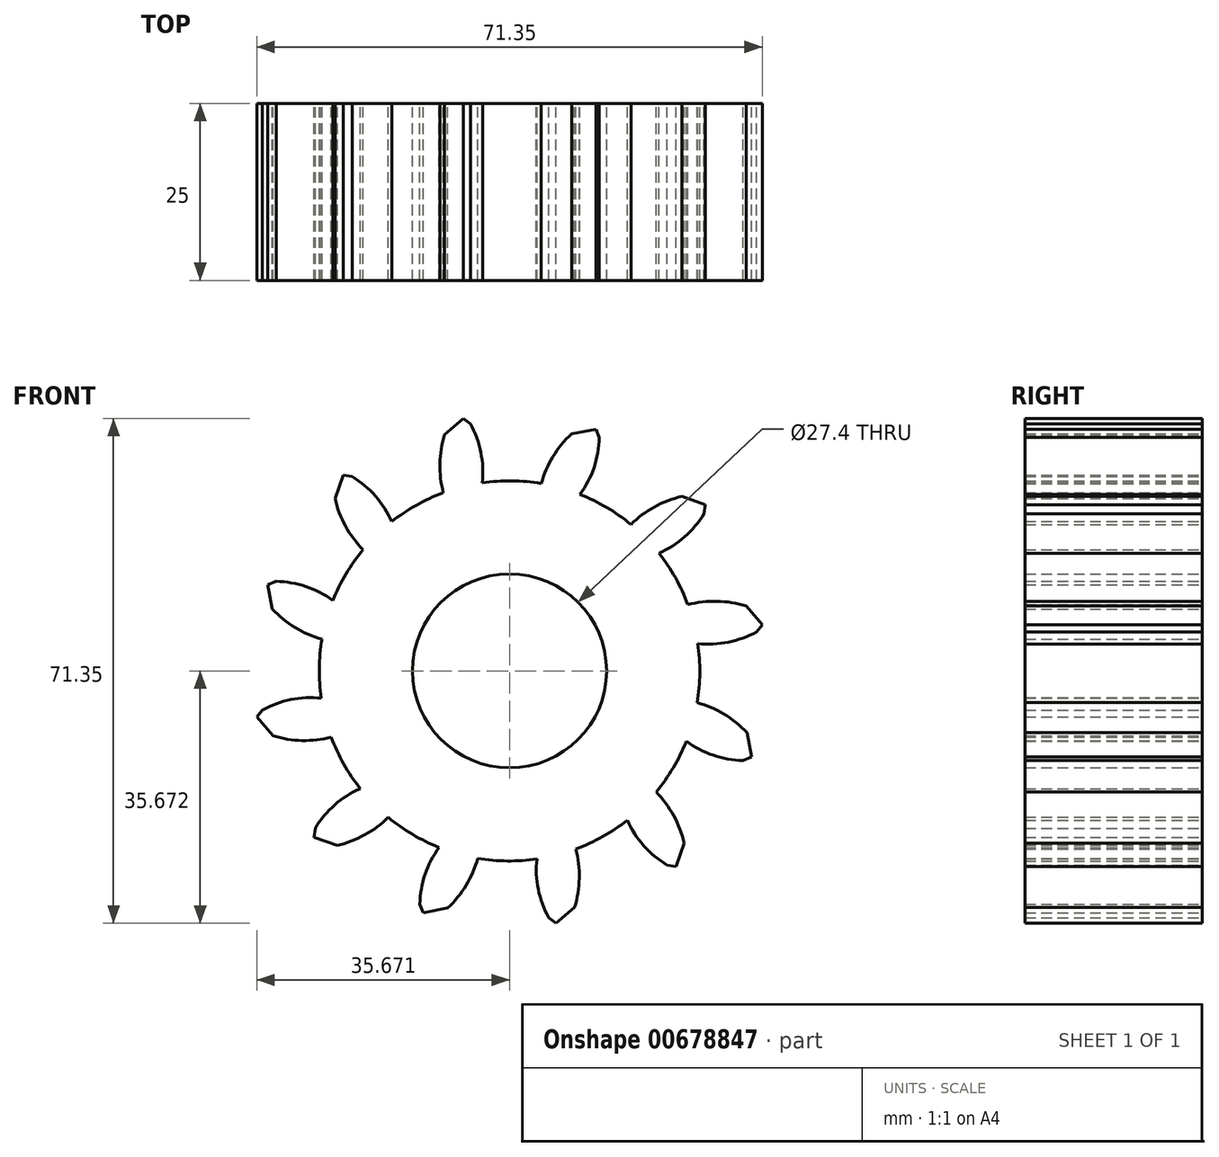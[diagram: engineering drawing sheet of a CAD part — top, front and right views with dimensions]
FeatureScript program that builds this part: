
annotation { "Feature Type Name" : "Feature", "Feature Type Description" : "" }
export const myFeature = defineFeature(function(context is Context, id is Id, definition is map)
    precondition{}
    {
        {
            var Q0;
            Q0=qCreatedBy(makeId("Front.planeOp"),FACE);
            var sketch = newSketch(context, id + "F0", { "sketchPlane" : qUnion([Q0])});
            skCircle(sketch, "E0", {"center": v(1.34, -11.12) * mm, "radius": 26.86 * mm, "construction": true});
            skCircle(sketch, "E1", {"center": v(1.34, -11.12) * mm, "radius": 29.34 * mm, "construction": true});
            skCircle(sketch, "E2", {"center": v(1.34, -11.12) * mm, "radius": 31.75 * mm, "construction": true});
            skLineSegment(sketch, "E3", {"start": v(-1.9, 18.04) * mm, "end": v(-78.16, 22.27) * mm, "construction": true});
            skLineSegment(sketch, "E4", {"start": v(-1.9, 18.04) * mm, "end": v(-73.04, 18.04) * mm, "construction": true});
            skCircle(sketch, "E5", {"center": v(1.34, -11.12) * mm, "radius": 28.93 * mm, "construction": true});
            skCircle(sketch, "E6", {"center": v(-1.9, 18.04) * mm, "radius": 7.3 * mm, "construction": true});
            skCircle(sketch, "E7", {"center": v(-9.18, 18.44) * mm, "radius": 7.3 * mm, "construction": true});
            skArc(sketch, "E8", {"start": v(-2.52, 15.46) * mm, "mid": v(-2.7, 19.74) * mm, "end": v(-4.18, 23.76) * mm});
            skArc(sketch, "E9", {"start": v(-7.84, 22.28) * mm, "mid": v(-8.5, 18.18) * mm, "end": v(-8.02, 14.06) * mm});
            skLineSegment(sketch, "E10", {"start": v(-7.84, 22.28) * mm, "end": v(-5.19, 24.56) * mm});
            skLineSegment(sketch, "E11", {"start": v(-5.19, 24.56) * mm, "end": v(-4.18, 23.76) * mm});
            skLineSegment(sketch, "E12.0", {"start": v(18.85, 9.47) * mm, "end": v(23, 5.06) * mm});
            skLineSegment(sketch, "E12.1", {"start": v(23, 5.06) * mm, "end": v(26.05, -0.16) * mm});
            skLineSegment(sketch, "E12.2", {"start": v(26.05, -0.16) * mm, "end": v(27.87, -5.94) * mm});
            skLineSegment(sketch, "E12.3", {"start": v(27.87, -5.94) * mm, "end": v(28.36, -11.97) * mm});
            skLineSegment(sketch, "E12.4", {"start": v(28.36, -11.97) * mm, "end": v(27.5, -17.96) * mm});
            skLineSegment(sketch, "E12.5", {"start": v(27.5, -17.96) * mm, "end": v(25.31, -23.6) * mm});
            skLineSegment(sketch, "E12.6", {"start": v(25.31, -23.6) * mm, "end": v(21.93, -28.63) * mm});
            skLineSegment(sketch, "E12.7", {"start": v(21.93, -28.63) * mm, "end": v(17.52, -32.77) * mm});
            skLineSegment(sketch, "E12.8", {"start": v(17.52, -32.77) * mm, "end": v(12.3, -35.83) * mm});
            skLineSegment(sketch, "E12.9", {"start": v(12.3, -35.83) * mm, "end": v(6.52, -37.65) * mm});
            skLineSegment(sketch, "E12.10", {"start": v(6.52, -37.65) * mm, "end": v(0.49, -38.13) * mm});
            skLineSegment(sketch, "E12.11", {"start": v(0.49, -38.13) * mm, "end": v(-5.5, -37.27) * mm});
            skLineSegment(sketch, "E12.12", {"start": v(-5.5, -37.27) * mm, "end": v(-11.15, -35.09) * mm});
            skLineSegment(sketch, "E12.13", {"start": v(-11.15, -35.09) * mm, "end": v(-16.17, -31.7) * mm});
            skLineSegment(sketch, "E12.14", {"start": v(-16.17, -31.7) * mm, "end": v(-20.31, -27.3) * mm});
            skLineSegment(sketch, "E12.15", {"start": v(-20.31, -27.3) * mm, "end": v(-23.37, -22.07) * mm});
            skLineSegment(sketch, "E12.16", {"start": v(-23.37, -22.07) * mm, "end": v(-25.19, -16.3) * mm});
            skLineSegment(sketch, "E12.17", {"start": v(-25.19, -16.3) * mm, "end": v(-25.68, -10.27) * mm});
            skLineSegment(sketch, "E12.18", {"start": v(-25.68, -10.27) * mm, "end": v(-24.8, -4.28) * mm});
            skLineSegment(sketch, "E12.19", {"start": v(-24.8, -4.28) * mm, "end": v(-22.63, 1.37) * mm});
            skLineSegment(sketch, "E12.20", {"start": v(-22.63, 1.37) * mm, "end": v(-19.25, 6.4) * mm});
            skLineSegment(sketch, "E12.21", {"start": v(-19.25, 6.4) * mm, "end": v(-14.84, 10.54) * mm});
            skLineSegment(sketch, "E12.22", {"start": v(-14.84, 10.54) * mm, "end": v(-9.61, 13.6) * mm});
            skLineSegment(sketch, "E12.25", {"start": v(2.2, 15.9) * mm, "end": v(8.18, 15.03) * mm});
            skLineSegment(sketch, "E12.26", {"start": v(8.18, 15.03) * mm, "end": v(13.83, 12.85) * mm});
            skLineSegment(sketch, "E12.27", {"start": v(13.83, 12.85) * mm, "end": v(18.85, 9.47) * mm});
            skPoint(sketch, "E12.0.midPoint", {"position": v(20.92, 7.27) * mm});
            skCircle(sketch, "E13", {"center": v(1.34, -11.12) * mm, "radius": 26.86 * mm});
            skCircle(sketch, "E14", {"center": v(1.34, -11.12) * mm, "radius": 38.98 * mm});
            skCircle(sketch, "E15", {"center": v(1.34, -11.12) * mm, "radius": 13.7 * mm});
            skSolve(sketch);
        }
        {
            var Q0;
            {var subQ0=sQuery(id+"F0.wireOp",EDGE,"E13");var subQ17=makeQuery(id+"F0.imprint","INTERSECT",VERTEX,{"derivedFrom":[sQuery(id+"F0.wireOp",EDGE,"E12.2"),subQ0]});Q0=makeQuery(id+"F0.imprint","IMPRINT",FACE,{"disambiguationData":[TD([[makeQuery(id+"F0.imprint","IMPRINT",EDGE,{"disambiguationData":[TD([[subQ17,1.0]])],"derivedFrom":subQ0}),1.0]])]});}
            var Q1;
            {var subQ1=sQuery(id+"F0.wireOp",EDGE,"E10");Q1=makeQuery(id+"F0.imprint","IMPRINT",FACE,{"disambiguationData":[TD([[makeQuery(id+"F0.imprint","IMPRINT",EDGE,{"derivedFrom":subQ1}),-1.0]])]});}
            extrude(context, id + "F1", {"entities" : qUnion([Q0, Q1]), "depth" : 25 * mm, "offsetDistance" : 25 * mm});
        }
        {
            var Q0;
            Q0=makeQuery(id+"F1.opExtrude","SWEPT_BODY",BODY,{"disambiguationData":[OSD([sQuery(id+"F0.wireOp",EDGE,"E8"),sQuery(id+"F0.wireOp",EDGE,"E9"),sQuery(id+"F0.wireOp",EDGE,"E10"),sQuery(id+"F0.wireOp",EDGE,"E11"),sQuery(id+"F0.wireOp",EDGE,"E12.23"),sQuery(id+"F0.wireOp",EDGE,"E12.24")])]});
            var Q1;
            Q1=makeQuery(id+"F1.opExtrude","SWEPT_FACE",FACE,{"disambiguationData":[OSD([sQuery(id+"F0.wireOp",EDGE,"E13")])]});
            circularPattern(context, id + "F2", {"operationType" : NewBodyOperationType.ADD, "entities" : qUnion([Q0]), "axis" : qUnion([Q1]), "angle" : 360 * degree, "instanceCount" : 12, "equalSpace" : true});
        }
    });
